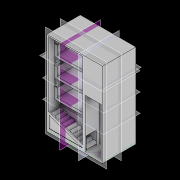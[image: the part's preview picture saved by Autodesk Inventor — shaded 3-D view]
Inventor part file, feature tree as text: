
AUTODESK INVENTOR PART (.ipt)
format: ipt  version: 2020 (Build 240168000, 168)  size: 1,709,056 bytes
history: native  units: mm
features: other x121, sketch x28, extrude x18, mirror x15, pattern_linear x14, plane x12, projected_geometry x8, hole x2, loft x2, chamfer x1
ambient origin geometry x8: Origin, YZ Plane, XZ Plane, XY Plane, X Axis, Y Axis, Z Axis, Center Point
bodies: Body1 (feature_tree), Body2 (feature_tree), Body3 (feature_tree), Body4 (feature_tree), Body5 (feature_tree), Body6 (feature_tree), Body7 (feature_tree), Body8 (feature_tree), Body9 (feature_tree), Body10 (feature_tree), Body11 (feature_tree), Body12 (feature_tree), Body13 (feature_tree), Body14 (feature_tree), Body15 (feature_tree), Body16 (feature_tree), Body17 (feature_tree), Body18 (feature_tree), Body19 (feature_tree), Body20 (feature_tree), Body21 (feature_tree), Body22 (feature_tree), Body23 (feature_tree), Body24 (feature_tree), Body25 (feature_tree), Body26 (feature_tree), Body27 (feature_tree), Body28 (feature_tree), Body29 (feature_tree), Body30 (feature_tree), Body31 (feature_tree), Body32 (feature_tree), Body33 (feature_tree), Body34 (feature_tree), Body35 (feature_tree), Body36 (feature_tree), Body37 (feature_tree), Body38 (feature_tree), Body39 (feature_tree), Body40 (feature_tree), Body41 (feature_tree), Body42 (feature_tree), Body43 (feature_tree), Body44 (feature_tree), Body45 (feature_tree)
feature tree (221):
  other  "實體1"
  extrude  "擠出1"  Depth=1200.0mm
  plane  "工作平面1"
  plane  "工作平面2"
  other  "分割1"
  plane  "工作平面3"
  extrude  "擠出3"  Depth=800.0mm
  plane  "工作平面6"
  plane  "工作平面7"
  extrude  "擠出4"  Depth=1820.0mm TaperAngle=0.0deg
  hole  "孔1"  [1 undecoded]
  pattern_linear  "矩形陣列1"  Spacing1=-80.0mm  [1 undecoded]
  pattern_linear  "矩形陣列2"  Spacing1=-30.0mm  [1 undecoded]
  pattern_linear  "矩形陣列3"  Count1=3  [1 undecoded]
  plane  "工作平面8"
  mirror  "鏡射1"
  mirror  "鏡射2"
  mirror  "鏡射3"
  extrude  "擠出5"  Depth=30.0mm
  plane  "工作平面9"
  other  "迴轉1"
  extrude  "擠出6"  Depth=30.0mm
  other  "迴轉2"
  plane  "工作平面10"
  extrude  "擠出7"  Depth=30.0mm
  loft  "斷面混成1"
  pattern_linear  "矩形陣列4"  Spacing1=-1230.0mm  [1 undecoded]
  pattern_linear  "矩形陣列5"  Count1=40 Spacing1=-345.0mm
  mirror  "鏡射4"
  mirror  "鏡射5"
  mirror  "鏡射6"
  pattern_linear  "矩形陣列6"  Count1=10  [1 undecoded]
  pattern_linear  "矩形陣列7"  Count1=2 Spacing1=0.0mm
  mirror  "鏡射7"
  mirror  "鏡射8"
  mirror  "鏡射9"
  sketch  "草圖13"
  extrude  "擠出8"  Depth=20.0mm
  extrude  "擠出9"  Depth=20.0mm
  extrude  "擠出10"  Depth=50.0mm
  extrude  "擠出11"  Depth=50.0mm
  other  "迴轉3"
  other  "迴轉4"
  plane  "工作平面11"
  extrude  "擠出12"  Depth=50.0mm
  loft  "斷面混成2"
  extrude  "擠出13"  Depth=20.0mm
  hole  "孔2"  [1 undecoded]
  pattern_linear  "矩形陣列8"  Spacing1=15.0mm  [1 undecoded]
  pattern_linear  "矩形陣列9"  Spacing1=11.0mm  [1 undecoded]
  pattern_linear  "矩形陣列10"  Spacing1=11.0mm  [1 undecoded]
  pattern_linear  "矩形陣列11"  Spacing1=11.0mm  [1 undecoded]
  mirror  "鏡射10"
  mirror  "鏡射11"
  mirror  "鏡射12"
  pattern_linear  "矩形陣列12"  Spacing1=11.0mm  [1 undecoded]
  pattern_linear  "矩形陣列13"  Spacing1=11.0mm  [1 undecoded]
  mirror  "鏡射13"
  mirror  "鏡射14"
  mirror  "鏡射15"
  extrude  "擠出14"  Depth=11.0mm
  plane  "工作平面12"
  other  "直接編輯1"
  other  "直接編輯2"
  other  "直接編輯3"
  other  "直接編輯4"
  other  "直接編輯5"
  other  "直接編輯6"
  sketch  "草圖26"
  extrude  "擠出15"  Depth=5.0mm TaperAngle=0.0deg
  chamfer  "倒角1"  Distance=10.0mm
  extrude  "擠出16"  Depth=15.0mm
  extrude  "擠出17"  Depth=2.5mm
  extrude  "擠出18"  TaperAngle=90.0deg  [1 undecoded]
  extrude  "擠出19"  Depth=10.0mm
  pattern_linear  "矩形陣列14"  Spacing1=1142.5mm  [1 undecoded]
  sketch  "草圖1"
  sketch  "草圖3"
  plane  "工作平面4"
  plane  "工作平面5"
  sketch  "草圖5"
  other  "實體4"
  sketch  "草圖6"
  other  "陣列 實體4:1"
  other  "實體5"
  other  "陣列 實體4:2"
  other  "實體6"
  other  "陣列 實體4:3"
  other  "實體7"
  other  "陣列 實體5:4"
  other  "實體8"
  other  "陣列 實體6:5"
  other  "實體9"
  sketch  "草圖7"
  other  "實體10"
  sketch  "草圖8"
  sketch  "草圖9"
  sketch  "草圖10"
  other  "實體11"
  sketch  "草圖11"
  projected_geometry  "投影迴路1"
  sketch  "草圖12"
  projected_geometry  "投影迴路2"
  other  "陣列 實體10:6"
  other  "實體12"
  other  "陣列 實體10:7"
  other  "實體13"
  other  "陣列 實體10:8"
  other  "實體14"
  other  "陣列 實體12:9"
  other  "實體15"
  other  "陣列 實體13:10"
  other  "實體16"
  other  "陣列 實體11:11"
  other  "實體17"
  other  "陣列 實體11:12"
  other  "實體18"
  other  "陣列 實體11:13"
  other  "實體19"
  other  "陣列 實體17:14"
  other  "實體20"
  other  "陣列 實體18:15"
  other  "實體21"
  sketch  "草圖14"
  projected_geometry  "投影迴路3"
  other  "實體22"
  sketch  "草圖15"
  sketch  "草圖16"
  sketch  "草圖17"
  projected_geometry  "投影迴路4"
  projected_geometry  "投影迴路5"
  projected_geometry  "投影迴路6"
  other  "實體23"
  sketch  "草圖18"
  sketch  "草圖19"
  other  "實體24"
  sketch  "草圖20"
  projected_geometry  "投影迴路7"
  sketch  "草圖21"
  sketch  "草圖22"
  sketch  "草圖23"
  other  "陣列 實體22:16"
  other  "實體25"
  other  "陣列 實體22:17"
  other  "實體26"
  other  "陣列 實體23:18"
  other  "實體27"
  other  "陣列 實體23:19"
  other  "實體28"
  other  "陣列 實體23:20"
  other  "實體29"
  other  "陣列 實體27:21"
  other  "實體30"
  other  "陣列 實體28:22"
  other  "實體31"
  other  "陣列 實體24:23"
  other  "實體32"
  other  "陣列 實體24:24"
  other  "實體33"
  other  "陣列 實體24:25"
  other  "實體34"
  other  "陣列 實體32:26"
  other  "實體35"
  other  "陣列 實體33:27"
  other  "實體36"
  sketch  "草圖24"
  sketch  "草圖27"
  sketch  "草圖28"
  sketch  "草圖29"
  sketch  "草圖30"
  projected_geometry  "投影迴路8"
  sketch  "草圖31"
  other  "實體37"
  other  "陣列 實體37:28"
  other  "實體38"
  other  "陣列 實體37:29"
  other  "實體39"
  other  "陣列 實體37:30"
  other  "實體40"
  other  "陣列 實體37:31"
  other  "實體41"
  other  "陣列 實體37:32"
  other  "實體42"
  other  "陣列 實體37:33"
  other  "實體43"
  other  "陣列 實體37:34"
  other  "實體44"
  other  "陣列 實體37:35"
  other  "實體45"
  other  "陣列 實體37:36"
  other  "實體46"
  other  "實體2"
  other  "實體3"
  other  "投影切割邊1"
  other  "投影切割邊2"
  other  "投影切割邊3"
  other  "投影切割邊4"
  other  "投影切割邊5"
  other  "投影切割邊6"
  other  "投影切割邊7"
  other  "投影切割邊8"
  other  "投影切割邊9"
  other  "投影切割邊10"
  other  "投影切割邊11"
  other  "投影切割邊12"
  other  "投影切割邊13"
  other  "投影切割邊14"
  other  "投影切割邊15"
  other  "投影切割邊16"
  other  "投影切割邊17"
  other  "移動1"
  other  "移動2"
  other  "移動3"
  other  "移動4"
  other  "移動5"
  other  "移動6"
  other  "投影切割邊18"
  other  "投影切割邊19"
  other  "投影切割邊20"
  other  "投影切割邊21"
  other  "投影切割邊22"
note: 15 required parameter values undecoded (feature->parameter linkage not recoverable at this tier; creation-order binding heuristic only, values carry confidence <= 0.55)
